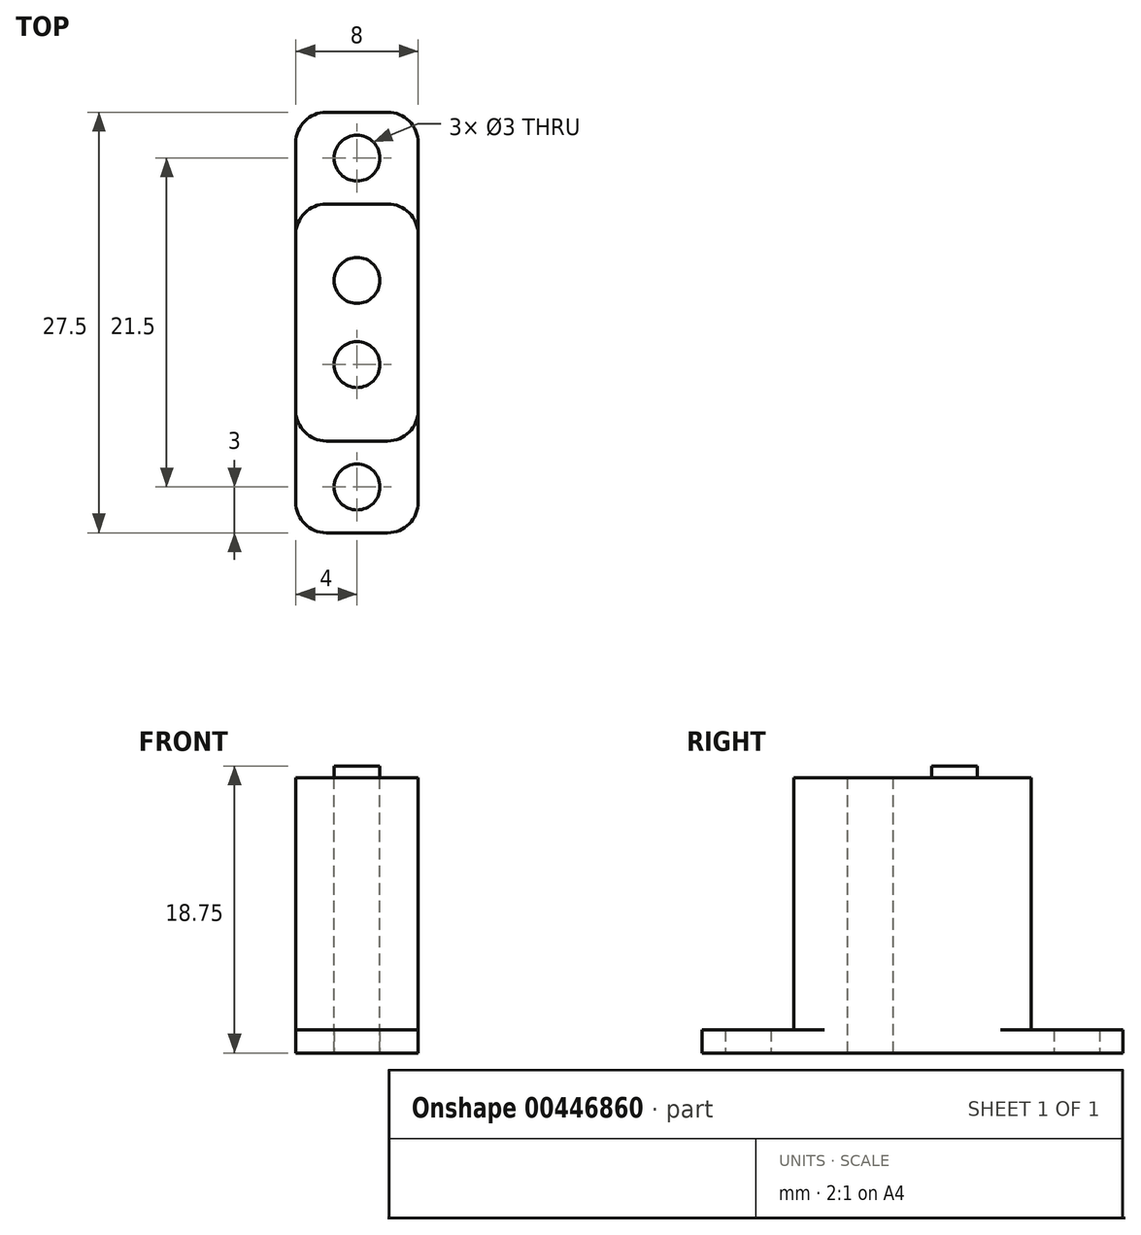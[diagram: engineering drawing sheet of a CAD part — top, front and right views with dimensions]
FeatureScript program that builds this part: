
annotation { "Feature Type Name" : "Feature", "Feature Type Description" : "" }
export const myFeature = defineFeature(function(context is Context, id is Id, definition is map)
    precondition{}
    {
        {
            var Q0;
            Q0=qCreatedBy(makeId("Top.planeOp"),FACE);
            var sketch = newSketch(context, id + "F0", { "sketchPlane" : qUnion([Q0])});
            skLineSegment(sketch, "E0.bottom", {"start": v(0, 0) * mm, "end": v(8, 0) * mm});
            skLineSegment(sketch, "E0.top", {"start": v(0, 15.5) * mm, "end": v(8, 15.5) * mm});
            skLineSegment(sketch, "E0.left", {"start": v(0, 0) * mm, "end": v(0, 15.5) * mm});
            skLineSegment(sketch, "E0.right", {"start": v(8, 0) * mm, "end": v(8, 15.5) * mm});
            skPoint(sketch, "E1", {"position": v(4, 5) * mm});
            skPoint(sketch, "E2", {"position": v(4, 10.5) * mm});
            skCircle(sketch, "E3", {"center": v(4, 10.5) * mm, "radius": 1.5 * mm});
            skSolve(sketch);
        }
        {
            var Q0;
            Q0=makeQuery(id+"F0.imprint","IMPRINT",FACE,{"disambiguationData":[TD([[makeQuery(id+"F0.imprint","IMPRINT",EDGE,{"derivedFrom":sQuery(id+"F0.wireOp",EDGE,"E0.bottom")}),1.0]])]});
            var Q1;
            Q1=makeQuery(id+"F0.imprint","IMPRINT",FACE,{"disambiguationData":[TD([[makeQuery(id+"F0.imprint","IMPRINT",EDGE,{"derivedFrom":sQuery(id+"F0.wireOp",EDGE,"E3")}),1.0]])]});
            extrude(context, id + "F1", {"entities" : qUnion([Q0, Q1]), "oppositeDirection" : true, "depth" : 18 * mm});
        }
        {
            var Q0;
            Q0=sQuery(id+"F0.wireOp",VERTEX,"E1");
            var Q1;
            Q1=makeQuery(id+"F1.opExtrude","SWEPT_BODY",BODY,{"disambiguationData":[OSD([sQuery(id+"F0.wireOp",EDGE,"E0.bottom"),sQuery(id+"F0.wireOp",EDGE,"E0.top"),sQuery(id+"F0.wireOp",EDGE,"E0.left"),sQuery(id+"F0.wireOp",EDGE,"E0.right")])]});
            hole(context, id + "F2", {"style" : HoleStyle.SIMPLE, "endStyle" : HoleEndStyle.THROUGH, "holeDiameter" : 3 * mm, "isTappedThrough" : true, "tappedDepth" : 12 * mm, "tapClearance" : 3, "locations" : qUnion([Q0]), "scope" : qUnion([Q1])});
        }
        {
            var Q0;
            Q0=makeQuery(id+"F0.imprint","IMPRINT",FACE,{"disambiguationData":[TD([[makeQuery(id+"F0.imprint","IMPRINT",EDGE,{"derivedFrom":sQuery(id+"F0.wireOp",EDGE,"E3")}),1.0]])]});
            extrude(context, id + "F3", {"entities" : qUnion([Q0]), "operationType" : NewBodyOperationType.ADD, "depth" : 0.75 * mm});
        }
        {
            var Q0;
            Q0=makeQuery(id+"F1.opExtrude","CAP_FACE",FACE,{"disambiguationData":[OSD([sQuery(id+"F0.wireOp",EDGE,"E0.bottom"),sQuery(id+"F0.wireOp",EDGE,"E0.top"),sQuery(id+"F0.wireOp",EDGE,"E0.left"),sQuery(id+"F0.wireOp",EDGE,"E0.right")])],"isStart":false});
            var sketch = newSketch(context, id + "F4", { "sketchPlane" : qUnion([Q0])});
            skLineSegment(sketch, "E4.bottom", {"start": v(0, -15.5) * mm, "end": v(8, -15.5) * mm});
            skLineSegment(sketch, "E4.top", {"start": v(0, -21.5) * mm, "end": v(8, -21.5) * mm});
            skLineSegment(sketch, "E4.left", {"start": v(0, -15.5) * mm, "end": v(0, -21.5) * mm});
            skLineSegment(sketch, "E4.right", {"start": v(8, -15.5) * mm, "end": v(8, -21.5) * mm});
            skLineSegment(sketch, "E5.bottom", {"start": v(8, 0) * mm, "end": v(0, 0) * mm});
            skLineSegment(sketch, "E5.top", {"start": v(8, 6) * mm, "end": v(0, 6) * mm});
            skLineSegment(sketch, "E5.left", {"start": v(8, 0) * mm, "end": v(8, 6) * mm});
            skLineSegment(sketch, "E5.right", {"start": v(0, 0) * mm, "end": v(0, 6) * mm});
            skPoint(sketch, "E6", {"position": v(4, -18.5) * mm});
            skPoint(sketch, "E6.positionSnap0", {"position": v(8, -18.5) * mm});
            skPoint(sketch, "E6.positionSnap1", {"position": v(4, -15.5) * mm});
            skPoint(sketch, "E7", {"position": v(4, 3) * mm});
            skPoint(sketch, "E7.positionSnap0", {"position": v(8, 3) * mm});
            skPoint(sketch, "E7.positionSnap1", {"position": v(4, 6) * mm});
            skSolve(sketch);
        }
        {
            var Q0;
            Q0=makeQuery(id+"F4.imprint","IMPRINT",FACE,{"disambiguationData":[TD([[makeQuery(id+"F4.imprint","IMPRINT",EDGE,{"derivedFrom":sQuery(id+"F4.wireOp",EDGE,"E5.bottom")}),1.0]])]});
            var Q1;
            Q1=makeQuery(id+"F4.imprint","IMPRINT",FACE,{"disambiguationData":[TD([[makeQuery(id+"F4.imprint","IMPRINT",EDGE,{"derivedFrom":sQuery(id+"F4.wireOp",EDGE,"E4.bottom")}),-1.0]])]});
            extrude(context, id + "F5", {"entities" : qUnion([Q0, Q1]), "operationType" : NewBodyOperationType.ADD, "oppositeDirection" : true, "depth" : 1.5 * mm});
        }
        {
            var Q0;
            Q0=sQuery(id+"F4.wireOp",VERTEX,"E7");
            var Q1;
            Q1=sQuery(id+"F4.wireOp",VERTEX,"E6");
            var Q2;
            Q2=makeQuery(id+"F1.opExtrude","SWEPT_BODY",BODY,{"disambiguationData":[OSD([sQuery(id+"F0.wireOp",EDGE,"E0.bottom"),sQuery(id+"F0.wireOp",EDGE,"E0.top"),sQuery(id+"F0.wireOp",EDGE,"E0.left"),sQuery(id+"F0.wireOp",EDGE,"E0.right")])]});
            hole(context, id + "F6", {"style" : HoleStyle.SIMPLE, "endStyle" : HoleEndStyle.THROUGH, "holeDiameter" : 3 * mm, "isTappedThrough" : true, "tappedDepth" : 12 * mm, "tapClearance" : 3, "locations" : qUnion([Q0, Q1]), "scope" : qUnion([Q2])});
        }
        {
            var Q0;
            Q0=makeQuery(id+"F1.opExtrude","SWEPT_EDGE",EDGE,{"disambiguationData":[OSD([sQuery(id+"F0.wireOp",EDGE,"E0.bottom"),sQuery(id+"F0.wireOp",EDGE,"E0.left")])]});
            var Q1;
            Q1=makeQuery(id+"F1.opExtrude","SWEPT_EDGE",EDGE,{"disambiguationData":[OSD([sQuery(id+"F0.wireOp",EDGE,"E0.bottom"),sQuery(id+"F0.wireOp",EDGE,"E0.right")])]});
            var Q2;
            Q2=makeQuery(id+"F1.opExtrude","SWEPT_EDGE",EDGE,{"disambiguationData":[OSD([sQuery(id+"F0.wireOp",EDGE,"E0.top"),sQuery(id+"F0.wireOp",EDGE,"E0.right")])]});
            var Q3;
            Q3=makeQuery(id+"F1.opExtrude","SWEPT_EDGE",EDGE,{"disambiguationData":[OSD([sQuery(id+"F0.wireOp",EDGE,"E0.top"),sQuery(id+"F0.wireOp",EDGE,"E0.left")])]});
            var Q4;
            Q4=makeQuery(id+"F5.opExtrude","SWEPT_EDGE",EDGE,{"disambiguationData":[OSD([sQuery(id+"F4.wireOp",EDGE,"E5.top"),sQuery(id+"F4.wireOp",EDGE,"E5.left")])]});
            var Q5;
            Q5=makeQuery(id+"F5.opExtrude","SWEPT_EDGE",EDGE,{"disambiguationData":[OSD([sQuery(id+"F4.wireOp",EDGE,"E5.top"),sQuery(id+"F4.wireOp",EDGE,"E5.right")])]});
            var Q6;
            Q6=makeQuery(id+"F5.opExtrude","SWEPT_EDGE",EDGE,{"disambiguationData":[OSD([sQuery(id+"F4.wireOp",EDGE,"E4.top"),sQuery(id+"F4.wireOp",EDGE,"E4.right")])]});
            var Q7;
            Q7=makeQuery(id+"F5.opExtrude","SWEPT_EDGE",EDGE,{"disambiguationData":[OSD([sQuery(id+"F4.wireOp",EDGE,"E4.top"),sQuery(id+"F4.wireOp",EDGE,"E4.left")])]});
            fillet(context, id + "F7", {"entities" : qUnion([Q0, Q1, Q2, Q3, Q4, Q5, Q6, Q7]), "radius" : 2 * mm, "tangentPropagation" : true, "allowEdgeOverflow" : false});
        }
    });
